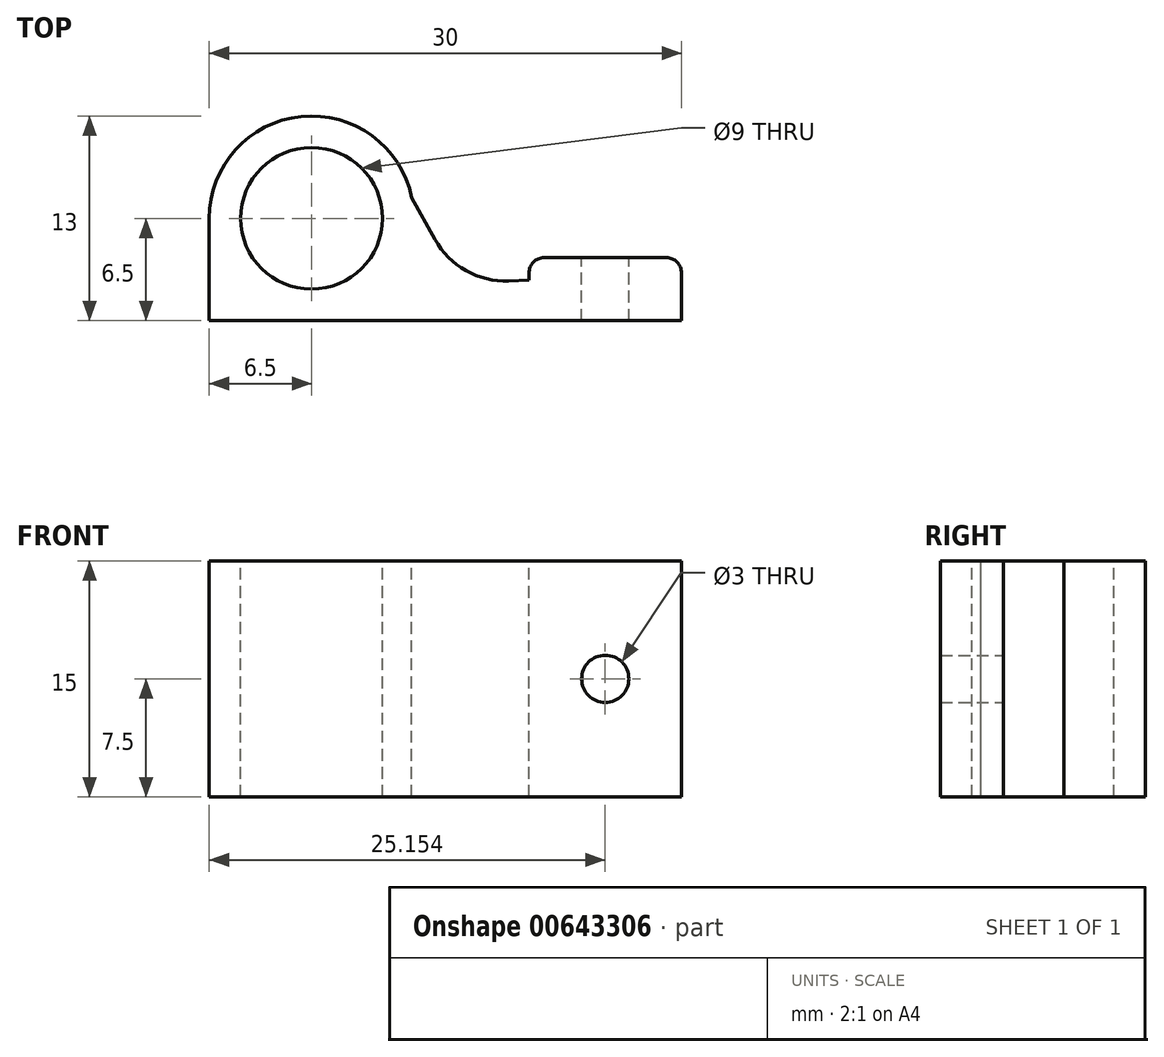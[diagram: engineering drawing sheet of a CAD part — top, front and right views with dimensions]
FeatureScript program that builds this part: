
annotation { "Feature Type Name" : "Feature", "Feature Type Description" : "" }
export const myFeature = defineFeature(function(context is Context, id is Id, definition is map)
    precondition{}
    {
        {
            var Q0;
            Q0=qCreatedBy(makeId("Top.planeOp"),FACE);
            var sketch = newSketch(context, id + "F0", { "sketchPlane" : qUnion([Q0])});
            skLineSegment(sketch, "E0.bottom", {"start": v(0, 0) * mm, "end": v(30, 0) * mm});
            skLineSegment(sketch, "E0.left", {"start": v(0, 0) * mm, "end": v(0, 6.5) * mm});
            skLineSegment(sketch, "E0.right", {"start": v(30, 0) * mm, "end": v(30, 4) * mm});
            skCircle(sketch, "E1", {"center": v(6.5, 6.5) * mm, "radius": 6.5 * mm});
            skCircle(sketch, "E2.0", {"center": v(6.5, 6.5) * mm, "radius": 4.5 * mm});
            skLineSegment(sketch, "E3", {"start": v(30, 4) * mm, "end": v(20.3, 4) * mm});
            skLineSegment(sketch, "E4", {"start": v(20.3, 4) * mm, "end": v(20.3, 2.58) * mm});
            skLineSegment(sketch, "E5", {"start": v(20.3, 2.58) * mm, "end": v(15.86, 2.4) * mm});
            skLineSegment(sketch, "E6", {"start": v(15.86, 2.4) * mm, "end": v(12.86, 7.82) * mm});
            skSolve(sketch);
        }
        {
            var Q0;
            {var subQ4=sQuery(id+"F0.wireOp",EDGE,"E0.right");Q0=makeQuery(id+"F0.imprint","IMPRINT",FACE,{"disambiguationData":[TD([[makeQuery(id+"F0.imprint","IMPRINT",EDGE,{"derivedFrom":subQ4}),1.0]])]});}
            var Q1;
            Q1=makeQuery(id+"F0.imprint","IMPRINT",FACE,{"disambiguationData":[TD([[makeQuery(id+"F0.imprint","IMPRINT",EDGE,{"derivedFrom":sQuery(id+"F0.wireOp",EDGE,"E2.0")}),-1.0]])]});
            var Q2;
            {var subQ0=sQuery(id+"F0.wireOp",EDGE,"E0.left");Q2=makeQuery(id+"F0.imprint","IMPRINT",FACE,{"disambiguationData":[TD([[makeQuery(id+"F0.imprint","IMPRINT",EDGE,{"derivedFrom":subQ0}),-1.0]])]});}
            var Q3;
            Q3=sQuery(id+"F0.wireOp",EDGE,"E2.0");
            var Q4;
            Q4=sQuery(id+"F0.wireOp",EDGE,"E1");
            var Q5;
            Q5=sQuery(id+"F0.wireOp",EDGE,"E5");
            var Q6;
            Q6=sQuery(id+"F0.wireOp",EDGE,"E6");
            var Q7;
            Q7=sQuery(id+"F0.wireOp",EDGE,"E0.left");
            var Q8;
            Q8=sQuery(id+"F0.wireOp",EDGE,"E4");
            var Q9;
            Q9=sQuery(id+"F0.wireOp",EDGE,"E0.bottom");
            var Q10;
            Q10=sQuery(id+"F0.wireOp",EDGE,"E3");
            var Q11;
            Q11=sQuery(id+"F0.wireOp",EDGE,"E0.right");
            extrude(context, id + "F1", {"entities" : qUnion([Q0, Q1, Q2]), "surfaceEntities" : qUnion([Q3, Q4, Q5, Q6, Q7, Q8, Q9, Q10, Q11]), "oppositeDirection" : true, "depth" : 15 * mm, "offsetDistance" : 25 * mm});
        }
        {
            var Q0;
            Q0=makeQuery(id+"F1.opExtrude","SWEPT_FACE",FACE,{"disambiguationData":[OSD([sQuery(id+"F0.wireOp",EDGE,"E3")])]});
            var sketch = newSketch(context, id + "F2", { "sketchPlane" : qUnion([Q0])});
            skLineSegment(sketch, "E7", {"start": v(-25.15, 0) * mm, "end": v(-25.15, -15) * mm, "construction": true});
            skLineSegment(sketch, "E8", {"start": v(-25.15, -7.5) * mm, "end": v(-30, -7.5) * mm, "construction": true});
            skCircle(sketch, "E9", {"center": v(-25.15, -7.5) * mm, "radius": 1.5 * mm});
            skSolve(sketch);
        }
        {
            var Q0;
            Q0=makeQuery(id+"F1.opExtrude","SWEPT_EDGE",EDGE,{"disambiguationData":[OSD([sQuery(id+"F0.wireOp",EDGE,"E5"),sQuery(id+"F0.wireOp",EDGE,"E6")])]});
            fillet(context, id + "F3", {"entities" : qUnion([Q0]), "radius" : 5.11 * mm, "tangentPropagation" : true, "allowEdgeOverflow" : false});
        }
        {
            var Q0;
            Q0=makeQuery(id+"F1.opExtrude","SWEPT_EDGE",EDGE,{"disambiguationData":[OSD([sQuery(id+"F0.wireOp",EDGE,"E0.right"),sQuery(id+"F0.wireOp",EDGE,"E3")])]});
            var Q1;
            Q1=makeQuery(id+"F1.opExtrude","SWEPT_EDGE",EDGE,{"disambiguationData":[OSD([sQuery(id+"F0.wireOp",EDGE,"E3"),sQuery(id+"F0.wireOp",EDGE,"E4")])]});
            fillet(context, id + "F4", {"entities" : qUnion([Q0, Q1]), "radius" : 0.97 * mm, "tangentPropagation" : true, "allowEdgeOverflow" : false});
        }
        {
            var Q0;
            Q0=makeQuery(id+"F2.imprint","IMPRINT",FACE,{"disambiguationData":[TD([[makeQuery(id+"F2.imprint","IMPRINT",EDGE,{"derivedFrom":sQuery(id+"F2.wireOp",EDGE,"E9")}),1.0]])]});
            var Q1;
            Q1=sQuery(id+"F2.wireOp",EDGE,"E9");
            extrude(context, id + "F5", {"entities" : qUnion([Q0]), "operationType" : NewBodyOperationType.REMOVE, "surfaceEntities" : qUnion([Q1]), "endBound" : BoundingType.UP_TO_NEXT, "oppositeDirection" : true, "depth" : 25 * mm, "offsetDistance" : 25 * mm});
        }
    });
